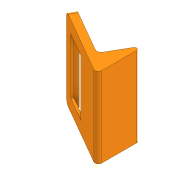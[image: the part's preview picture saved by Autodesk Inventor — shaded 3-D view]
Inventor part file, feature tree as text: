
AUTODESK INVENTOR PART (.ipt)
format: ipt  version: 2020.3 (Build 243373000, 373)  size: 194,560 bytes
history: native  units: mm
features: sketch x5, extrude x4, fillet x4, other x1
ambient origin geometry x8: Origin, YZ Plane, XZ Plane, XY Plane, X Axis, Y Axis, Z Axis, Center Point
bodies: Solid1 (feature_tree)
feature tree (14):
  extrude  "Extrusion1"  Depth=72.0mm
  extrude  "Extrusion2"  Depth=6.5mm
  extrude  "Extrusion3"  Depth=25.17mm
  fillet  "Fillet1"  Radius=50.25mm
  fillet  "Fillet2"  Radius=10.0mm
  fillet  "Fillet3"  Radius=7.0mm
  fillet  "Fillet4"  Radius=32.0mm
  extrude  "Extrusion4"  Depth=2.66mm
  sketch  "Sketch5"  dims[d14=4.5mm d15=0.0mm d16=3.0mm d17=2.0mm d18=4.0mm d19=90.0deg d20=4.0mm d21=3.1mm d22=16.41mm d23=3.5mm d24=3.1mm d25=31.0mm d26=3.2mm d27=38.0mm d28=3.2mm d29=38.0mm d30=4.5mm d31=0.0mm]
  sketch  "Sketch1"  dims[d0=72.0mm d1=50.0mm]
  sketch  "Sketch2"  dims[d2=60.0deg d3=6.5mm]
  sketch  "Sketch3"  dims[d4=72.0mm d5=0.0mm d6=25.17mm d7=50.25mm d8=10.0mm d9=7.0mm d10=0.0mm d11=32.0mm]
  sketch  "Sketch4"  dims[d12=65.0mm d13=2.66mm]
  other  "Image1"
